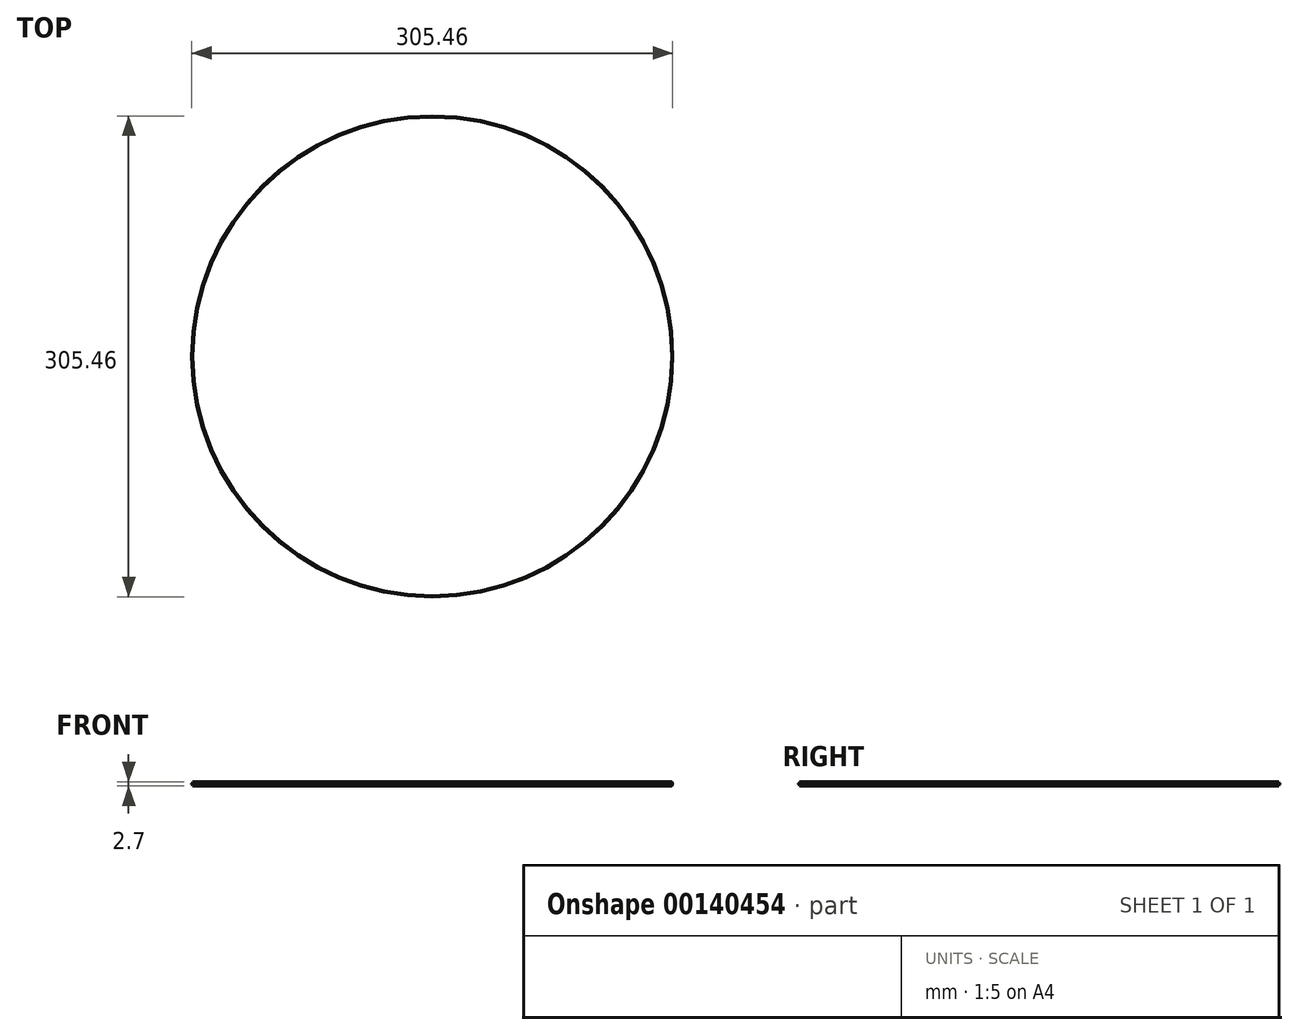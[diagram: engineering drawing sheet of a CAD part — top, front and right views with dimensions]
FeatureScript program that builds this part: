
annotation { "Feature Type Name" : "Feature", "Feature Type Description" : "" }
export const myFeature = defineFeature(function(context is Context, id is Id, definition is map)
    precondition{}
    {
        {
            var Q0;
            Q0=qCreatedBy(makeId("Front.planeOp"),FACE);
            var sketch = newSketch(context, id + "F0", { "sketchPlane" : qUnion([Q0])});
            skLineSegment(sketch, "E0", {"start": v(-152.1, 6.54) * mm, "end": v(-20.18, 6.54) * mm});
            skLineSegment(sketch, "E1", {"start": v(0, 30.8) * mm, "end": v(0, -118.37) * mm});
            skLineSegment(sketch, "E2", {"start": v(-19.86, 6.42) * mm, "end": v(-12, -0.13) * mm});
            skLineSegment(sketch, "E3.0", {"start": v(-154.43, 7.69) * mm, "end": v(-152.73, 7.69) * mm});
            skLineSegment(sketch, "E4", {"start": v(-154.66, 7.61) * mm, "end": v(-164.14, 0.74) * mm});
            skPoint(sketch, "E5.visualSharp", {"position": v(-152.9, 6.54) * mm});
            skArc(sketch, "E5.filletArc", {"start": v(-152.4, 6.79) * mm, "mid": v(-152.3, 6.6) * mm, "end": v(-152.1, 6.54) * mm});
            skLineSegment(sketch, "E6", {"start": v(-152.53, 7.52) * mm, "end": v(-152.4, 6.79) * mm});
            skPoint(sketch, "E7.visualSharp", {"position": v(-152.56, 7.69) * mm});
            skArc(sketch, "E7.filletArc", {"start": v(-152.53, 7.52) * mm, "mid": v(-152.6, 7.64) * mm, "end": v(-152.73, 7.69) * mm});
            skPoint(sketch, "E8.visualSharp", {"position": v(-154.56, 7.69) * mm});
            skArc(sketch, "E8.filletArc", {"start": v(-154.43, 7.69) * mm, "mid": v(-154.55, 7.67) * mm, "end": v(-154.66, 7.61) * mm});
            skPoint(sketch, "E9.visualSharp", {"position": v(-20, 6.54) * mm});
            skArc(sketch, "E9.filletArc", {"start": v(-19.86, 6.42) * mm, "mid": v(-20.01, 6.5) * mm, "end": v(-20.18, 6.54) * mm});
            skLineSegment(sketch, "E10", {"start": v(-164.17, -4.7) * mm, "end": v(-194.17, -4.7) * mm});
            skLineSegment(sketch, "E11.0", {"start": v(-10, -0.13) * mm, "end": v(-10, -32.31) * mm});
            skLineSegment(sketch, "E12.0", {"start": v(-194.17, -4.7) * mm, "end": v(-194.17, -32.31) * mm});
            skPoint(sketch, "E13.endSnap0", {"position": v(-154.55, 7.67) * mm});
            skLineSegment(sketch, "E14.0", {"start": v(-164.14, 0.74) * mm, "end": v(-164.17, -4.7) * mm});
            skLineSegment(sketch, "E15.0", {"start": v(-194.17, -32.31) * mm, "end": v(-10, -32.31) * mm});
            skPoint(sketch, "E16.orphan", {"position": v(-194.17, -4.7) * mm});
            skPoint(sketch, "E17.orphan", {"position": v(-194.17, 7.31) * mm});
            skLineSegment(sketch, "E18.0", {"start": v(-154.84, 7.86) * mm, "end": v(-164.24, 1.04) * mm});
            skLineSegment(sketch, "E19.0", {"start": v(-152.1, 6.84) * mm, "end": v(-20.18, 6.84) * mm});
            skArc(sketch, "E20.0", {"start": v(-154.43, 7.99) * mm, "mid": v(-154.64, 7.95) * mm, "end": v(-154.84, 7.86) * mm});
            skLineSegment(sketch, "E21.0", {"start": v(-154.43, 7.99) * mm, "end": v(-152.73, 7.99) * mm});
            skLineSegment(sketch, "E22.0", {"start": v(-152.23, 7.57) * mm, "end": v(-152.1, 6.84) * mm});
            skArc(sketch, "E23.0", {"start": v(-152.23, 7.57) * mm, "mid": v(-152.4, 7.87) * mm, "end": v(-152.73, 7.99) * mm});
            skPoint(sketch, "E24.orphan", {"position": v(0, -33.1) * mm});
            skLineSegment(sketch, "E25", {"start": v(-12, -0.13) * mm, "end": v(-10, -0.13) * mm});
            skLineSegment(sketch, "E26.0", {"start": v(-19.67, 6.65) * mm, "end": v(-11.8, 0.1) * mm});
            skArc(sketch, "E27.0", {"start": v(-19.67, 6.65) * mm, "mid": v(-19.9, 6.8) * mm, "end": v(-20.18, 6.84) * mm});
            skPoint(sketch, "E28.orphan", {"position": v(-194.17, -56.66) * mm});
            skLineSegment(sketch, "E29.0", {"start": v(-175.89, 8.19) * mm, "end": v(-152.8, 8.19) * mm, "construction": true});
            skArc(sketch, "E30.MirrorCS", {"start": v(-19.86, 9.95) * mm, "mid": v(-20.01, 9.87) * mm, "end": v(-20.18, 9.84) * mm});
            skArc(sketch, "E31.MirrorCS", {"start": v(-19.67, 9.72) * mm, "mid": v(-19.9, 9.59) * mm, "end": v(-20.18, 9.54) * mm});
            skLineSegment(sketch, "E32.MirrorCS", {"start": v(-19.86, 9.95) * mm, "end": v(-12, 16.5) * mm});
            skLineSegment(sketch, "E33.MirrorCS", {"start": v(-19.67, 9.72) * mm, "end": v(-11.8, 16.27) * mm});
            skLineSegment(sketch, "E34.MirrorCS", {"start": v(-12, 16.5) * mm, "end": v(-10, 16.5) * mm});
            skPoint(sketch, "E35.MirrorP", {"position": v(-20, 9.84) * mm});
            skLineSegment(sketch, "E36.MirrorCS", {"start": v(-194.17, 48.69) * mm, "end": v(-10, 48.69) * mm});
            skLineSegment(sketch, "E37.MirrorCS", {"start": v(-152.1, 9.54) * mm, "end": v(-20.18, 9.54) * mm});
            skLineSegment(sketch, "E38.MirrorCS", {"start": v(-10, 16.5) * mm, "end": v(-10, 48.69) * mm});
            skLineSegment(sketch, "E39.MirrorCS", {"start": v(-152.1, 9.84) * mm, "end": v(-20.18, 9.84) * mm});
            skPoint(sketch, "E40.MirrorP", {"position": v(0, 49.48) * mm});
            skLineSegment(sketch, "E41.MirrorCS", {"start": v(0, -14.42) * mm, "end": v(0, 134.75) * mm});
            skLineSegment(sketch, "E42.MirrorCS", {"start": v(-152.23, 8.8) * mm, "end": v(-152.1, 9.54) * mm});
            skLineSegment(sketch, "E43.MirrorCS", {"start": v(-154.43, 8.69) * mm, "end": v(-152.73, 8.69) * mm});
            skArc(sketch, "E44.MirrorCS", {"start": v(-152.23, 8.8) * mm, "mid": v(-152.4, 8.5) * mm, "end": v(-152.73, 8.39) * mm});
            skArc(sketch, "E45.MirrorCS", {"start": v(-152.4, 9.6) * mm, "mid": v(-152.3, 9.77) * mm, "end": v(-152.1, 9.84) * mm});
            skArc(sketch, "E46.MirrorCS", {"start": v(-154.43, 8.69) * mm, "mid": v(-154.55, 8.7) * mm, "end": v(-154.66, 8.76) * mm});
            skLineSegment(sketch, "E47.MirrorCS", {"start": v(-152.53, 8.85) * mm, "end": v(-152.4, 9.6) * mm});
            skArc(sketch, "E48.MirrorCS", {"start": v(-154.43, 8.39) * mm, "mid": v(-154.64, 8.42) * mm, "end": v(-154.84, 8.52) * mm});
            skArc(sketch, "E49.MirrorCS", {"start": v(-152.53, 8.85) * mm, "mid": v(-152.6, 8.74) * mm, "end": v(-152.73, 8.69) * mm});
            skLineSegment(sketch, "E50.MirrorCS", {"start": v(-154.43, 8.39) * mm, "end": v(-152.73, 8.39) * mm});
            skLineSegment(sketch, "E51.MirrorCS", {"start": v(-154.84, 8.52) * mm, "end": v(-164.24, 15.34) * mm});
            skLineSegment(sketch, "E52.MirrorCS", {"start": v(-164.14, 15.64) * mm, "end": v(-164.17, 21.08) * mm});
            skLineSegment(sketch, "E53.MirrorCS", {"start": v(-154.66, 8.76) * mm, "end": v(-164.14, 15.64) * mm});
            skPoint(sketch, "E54.MirrorP", {"position": v(-154.56, 8.69) * mm});
            skPoint(sketch, "E55.MirrorP", {"position": v(-194.17, 9.06) * mm});
            skPoint(sketch, "E56.MirrorP", {"position": v(-154.55, 8.7) * mm});
            skLineSegment(sketch, "E57.MirrorCS", {"start": v(-152.1, 9.54) * mm, "end": v(-20.3, 9.54) * mm});
            skPoint(sketch, "E58.MirrorP", {"position": v(-152.9, 9.84) * mm});
            skPoint(sketch, "E59.MirrorP", {"position": v(-194.17, 73.04) * mm});
            skLineSegment(sketch, "E60.MirrorCS", {"start": v(-164.17, 21.08) * mm, "end": v(-194.17, 21.08) * mm});
            skLineSegment(sketch, "E61.MirrorCS", {"start": v(-194.17, 21.08) * mm, "end": v(-194.17, 48.69) * mm});
            skLineSegment(sketch, "E62.MirrorCS", {"start": v(-152.1, 6.84) * mm, "end": v(-20.3, 6.84) * mm});
            skPoint(sketch, "E63.MirrorP", {"position": v(-194.17, 21.09) * mm});
            skPoint(sketch, "E64.MirrorP", {"position": v(-152.56, 8.69) * mm});
            skPoint(sketch, "E65.orphan", {"position": v(-152.31, 8.35) * mm});
            skPoint(sketch, "E66.orphan", {"position": v(-152.31, 8.02) * mm});
            skLineSegment(sketch, "E67", {"start": v(-152.73, 8.39) * mm, "end": v(-152.73, 7.99) * mm});
            skPoint(sketch, "E68.orphan", {"position": v(-20.3, 9.54) * mm});
            skPoint(sketch, "E69.orphan", {"position": v(-20.3, 6.84) * mm});
            skLineSegment(sketch, "E70", {"start": v(-20.18, 9.54) * mm, "end": v(0, 9.54) * mm});
            skLineSegment(sketch, "E71", {"start": v(-20.18, 6.84) * mm, "end": v(0, 6.84) * mm});
            skSolve(sketch);
        }
        {
            var Q0;
            Q0=makeQuery(id+"F0.imprint","IMPRINT",FACE,{"disambiguationData":[TD([[makeQuery(id+"F0.imprint","IMPRINT",EDGE,{"derivedFrom":sQuery(id+"F0.wireOp",EDGE,"E19.0")}),1.0]])]});
            var Q1;
            Q1=sQuery(id+"F0.wireOp",EDGE,"E1");
            revolve(context, id + "F1", {"entities" : qUnion([Q0]), "axis" : qUnion([Q1]), "revolveType" : RevolveType.FULL});
        }
    });
